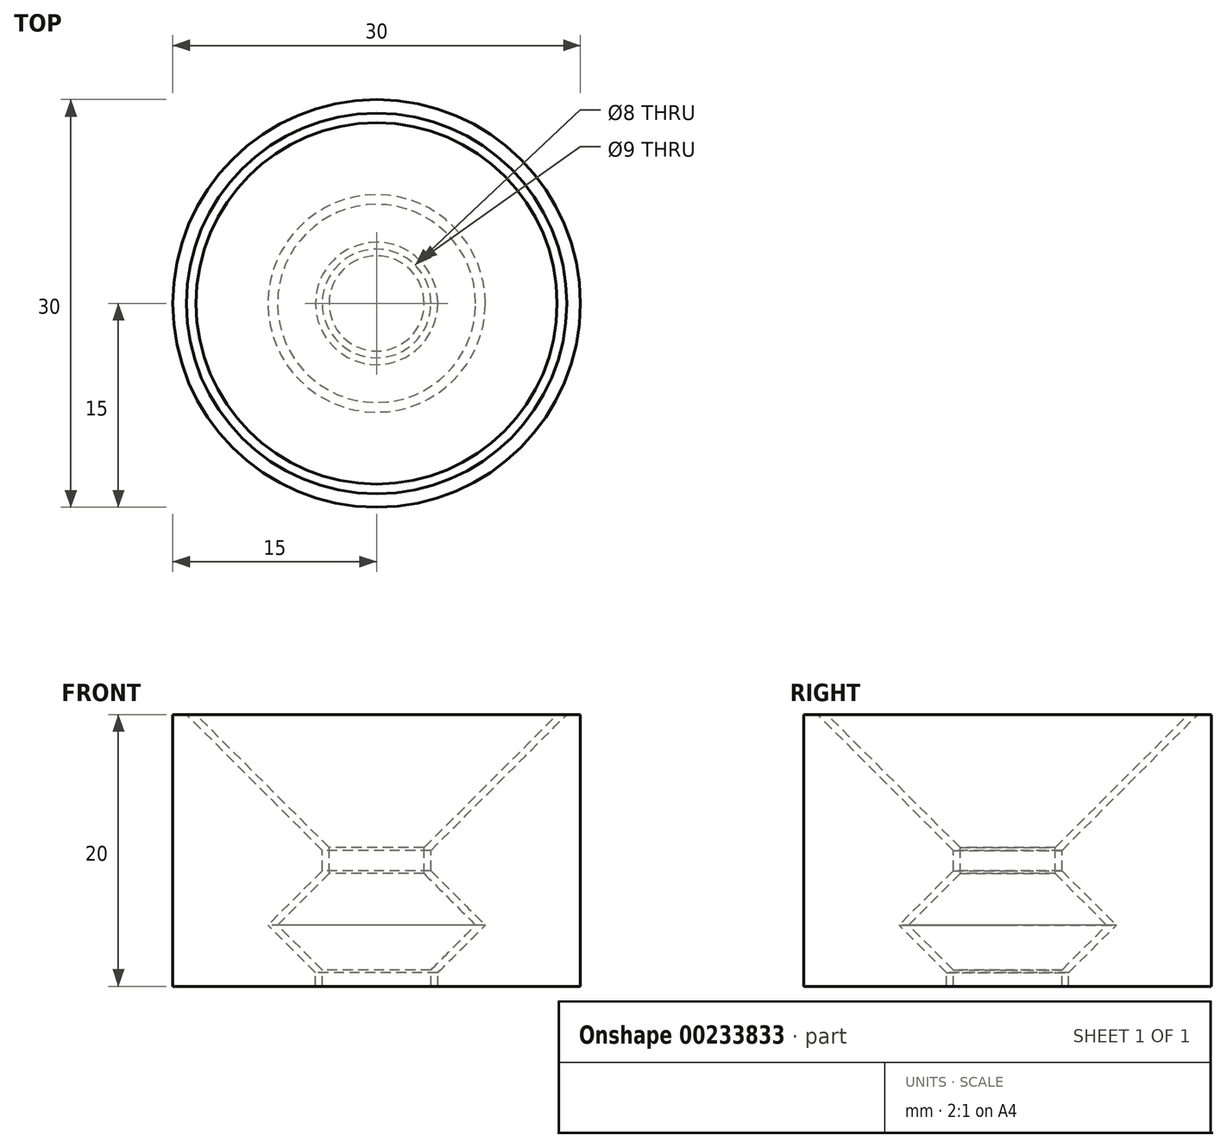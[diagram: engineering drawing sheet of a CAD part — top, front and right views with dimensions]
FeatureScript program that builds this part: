
annotation { "Feature Type Name" : "Feature", "Feature Type Description" : "" }
export const myFeature = defineFeature(function(context is Context, id is Id, definition is map)
    precondition{}
    {
        {
            var Q0;
            Q0=qCreatedBy(makeId("Front.planeOp"),FACE);
            var sketch = newSketch(context, id + "F0", { "sketchPlane" : qUnion([Q0])});
            skLineSegment(sketch, "E0.bottom", {"start": v(0, 0) * mm, "end": v(15, 0) * mm});
            skLineSegment(sketch, "E0.top", {"start": v(0, -20) * mm, "end": v(15, -20) * mm});
            skLineSegment(sketch, "E0.left", {"start": v(0, 0) * mm, "end": v(0, -20) * mm, "construction": true});
            skLineSegment(sketch, "E0.right", {"start": v(15, 0) * mm, "end": v(15, -20) * mm});
            skLineSegment(sketch, "E1", {"start": v(3.5, -20) * mm, "end": v(4.5, -19) * mm, "construction": true});
            skLineSegment(sketch, "E2", {"start": v(8, -15.5) * mm, "end": v(4, -11.5) * mm});
            skLineSegment(sketch, "E3", {"start": v(2.5, -10) * mm, "end": v(7.8, -10) * mm, "construction": true});
            skLineSegment(sketch, "E4", {"start": v(4.5, -19) * mm, "end": v(4.5, -20) * mm});
            skLineSegment(sketch, "E5", {"start": v(4.5, -19) * mm, "end": v(7, -16.5) * mm});
            skLineSegment(sketch, "E6", {"start": v(4, -11.5) * mm, "end": v(4, -10) * mm});
            skLineSegment(sketch, "E7.trimOffspring", {"start": v(4, -10) * mm, "end": v(14, 0) * mm});
            skLineSegment(sketch, "E8", {"start": v(7, -16.5) * mm, "end": v(8, -15.5) * mm});
            skPoint(sketch, "E8.endSnap0", {"position": v(8, -16.5) * mm});
            skPoint(sketch, "E9.orphan", {"position": v(9, -16.5) * mm});
            skSolve(sketch);
        }
        {
            var Q0;
            Q0=qCreatedBy(makeId("Front.planeOp"),FACE);
            var sketch = newSketch(context, id + "F1", { "sketchPlane" : qUnion([Q0])});
            skLineSegment(sketch, "E10.0", {"start": v(4, -11.5) * mm, "end": v(4, -10) * mm, "construction": true});
            skLineSegment(sketch, "E10.1", {"start": v(4.5, -19) * mm, "end": v(7, -16.5) * mm, "construction": true});
            skLineSegment(sketch, "E10.2", {"start": v(8, -15.5) * mm, "end": v(4, -11.5) * mm, "construction": true});
            skLineSegment(sketch, "E10.3", {"start": v(2.5, -10) * mm, "end": v(7.8, -10) * mm, "construction": true});
            skLineSegment(sketch, "E10.4", {"start": v(4, -10) * mm, "end": v(14, 0) * mm, "construction": true});
            skLineSegment(sketch, "E10.5", {"start": v(0, 0) * mm, "end": v(0, -20) * mm, "construction": true});
            skLineSegment(sketch, "E10.6", {"start": v(15, 0) * mm, "end": v(15, -20) * mm, "construction": true});
            skLineSegment(sketch, "E10.7", {"start": v(0, 0) * mm, "end": v(15, 0) * mm, "construction": true});
            skLineSegment(sketch, "E10.8", {"start": v(0, -20) * mm, "end": v(15, -20) * mm, "construction": true});
            skLineSegment(sketch, "E10.9", {"start": v(4.5, -19) * mm, "end": v(4.5, -20) * mm, "construction": true});
            skLineSegment(sketch, "E10.10", {"start": v(3.5, -20) * mm, "end": v(4.5, -19) * mm, "construction": true});
            skLineSegment(sketch, "E10.11", {"start": v(7, -16.5) * mm, "end": v(8, -15.5) * mm, "construction": true});
            skLineSegment(sketch, "E11.0", {"start": v(3.5, -9.8) * mm, "end": v(13.3, 0) * mm});
            skLineSegment(sketch, "E11.1", {"start": v(4, -18.8) * mm, "end": v(4, -20) * mm});
            skLineSegment(sketch, "E11.2", {"start": v(4, -18.8) * mm, "end": v(7.3, -15.5) * mm});
            skLineSegment(sketch, "E11.3", {"start": v(7.3, -15.5) * mm, "end": v(3.5, -11.7) * mm});
            skLineSegment(sketch, "E11.4", {"start": v(3.5, -11.7) * mm, "end": v(3.5, -9.8) * mm});
            skLineSegment(sketch, "E12", {"start": v(4, -20) * mm, "end": v(0, -20) * mm});
            skLineSegment(sketch, "E13", {"start": v(13.3, 0) * mm, "end": v(0, 0) * mm});
            skLineSegment(sketch, "E14", {"start": v(0, 0) * mm, "end": v(0, -20) * mm});
            skSolve(sketch);
        }
        {
            var Q0;
            {var subQ0=sQuery(id+"F0.wireOp",EDGE,"E0.right");Q0=makeQuery(id+"F0.imprint","IMPRINT",FACE,{"disambiguationData":[TD([[makeQuery(id+"F0.imprint","IMPRINT",EDGE,{"derivedFrom":subQ0}),-1.0]])]});}
            var Q1;
            Q1=makeQuery(id+"F1.imprint","IMPRINT",FACE,{"disambiguationData":[TD([[makeQuery(id+"F1.imprint","IMPRINT",EDGE,{"derivedFrom":sQuery(id+"F1.wireOp",EDGE,"E11.0")}),1.0]])]});
            var Q2;
            Q2=sQuery(id+"F1.wireOp",EDGE,"E14");
            revolve(context, id + "F2", {"entities" : qUnion([Q0, Q1]), "axis" : qUnion([Q2]), "revolveType" : RevolveType.FULL});
        }
    });
